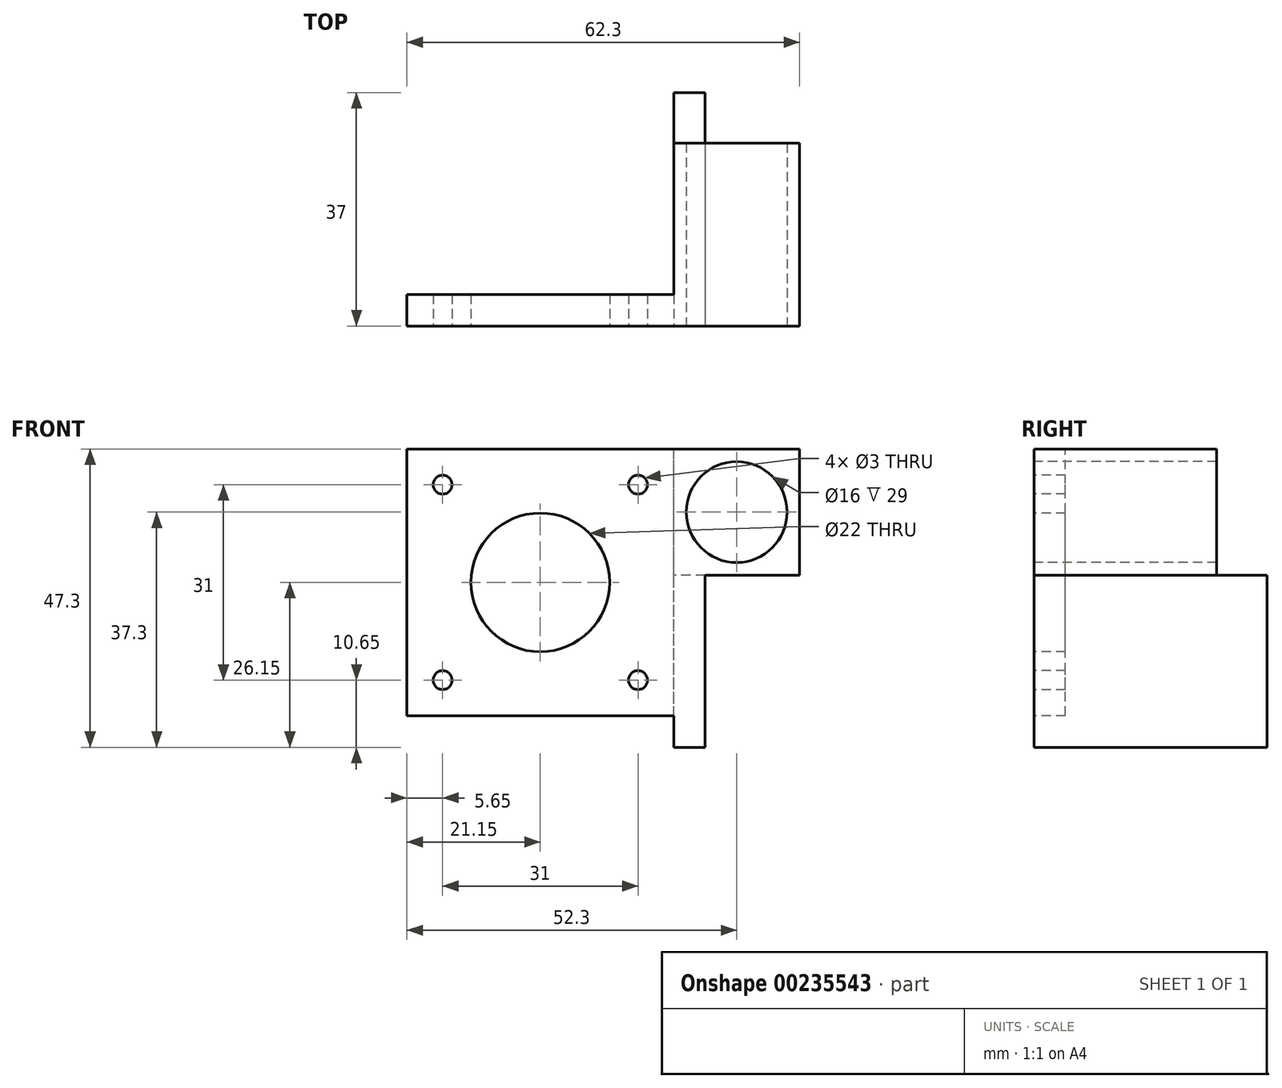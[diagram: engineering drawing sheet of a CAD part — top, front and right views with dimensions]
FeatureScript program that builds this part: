
annotation { "Feature Type Name" : "Feature", "Feature Type Description" : "" }
export const myFeature = defineFeature(function(context is Context, id is Id, definition is map)
    precondition{}
    {
        {
            var Q0;
            Q0=qCreatedBy(makeId("Front.planeOp"),FACE);
            var sketch = newSketch(context, id + "F0", { "sketchPlane" : qUnion([Q0])});
            skLineSegment(sketch, "E0.bottom", {"start": v(21.15, -21.15) * mm, "end": v(-21.15, -21.15) * mm});
            skLineSegment(sketch, "E0.top", {"start": v(20.15, 21.15) * mm, "end": v(-21.15, 21.15) * mm});
            skLineSegment(sketch, "E0.left", {"start": v(21.15, -21.15) * mm, "end": v(21.15, 20.15) * mm});
            skLineSegment(sketch, "E0.right", {"start": v(-21.15, -21.15) * mm, "end": v(-21.15, 21.15) * mm});
            skPoint(sketch, "E0.middle", {"position": v(0, 0) * mm});
            skLineSegment(sketch, "E1.bottom", {"start": v(15.5, -15.5) * mm, "end": v(-15.5, -15.5) * mm});
            skLineSegment(sketch, "E1.top", {"start": v(15.5, 15.5) * mm, "end": v(-15.5, 15.5) * mm});
            skLineSegment(sketch, "E1.left", {"start": v(15.5, -15.5) * mm, "end": v(15.5, 15.5) * mm});
            skLineSegment(sketch, "E1.right", {"start": v(-15.5, -15.5) * mm, "end": v(-15.5, 15.5) * mm});
            skCircle(sketch, "E2", {"center": v(-15.5, 15.5) * mm, "radius": 1.5 * mm});
            skCircle(sketch, "E3", {"center": v(15.5, 15.5) * mm, "radius": 1.5 * mm});
            skCircle(sketch, "E4", {"center": v(-15.5, -15.5) * mm, "radius": 1.5 * mm});
            skCircle(sketch, "E5", {"center": v(15.5, -15.5) * mm, "radius": 1.5 * mm});
            skLineSegment(sketch, "E6.bottom", {"start": v(-21.15, -21.15) * mm, "end": v(21.15, -21.15) * mm});
            skLineSegment(sketch, "E6.top", {"start": v(-21.15, -26.15) * mm, "end": v(21.15, -26.15) * mm});
            skLineSegment(sketch, "E6.left", {"start": v(-21.15, -21.15) * mm, "end": v(-21.15, -26.15) * mm});
            skLineSegment(sketch, "E6.right", {"start": v(21.15, -21.15) * mm, "end": v(21.15, -26.15) * mm});
            skCircle(sketch, "E7", {"center": v(0, 0) * mm, "radius": 11 * mm});
            skLineSegment(sketch, "E8.bottom", {"start": v(-21.15, 21.15) * mm, "end": v(20.15, 21.15) * mm});
            skLineSegment(sketch, "E8.top", {"start": v(-21.15, 26.15) * mm, "end": v(20.15, 26.15) * mm});
            skLineSegment(sketch, "E8.left", {"start": v(-21.15, 21.15) * mm, "end": v(-21.15, 26.15) * mm});
            skLineSegment(sketch, "E9.top", {"start": v(21.15, -26.15) * mm, "end": v(26.15, -26.15) * mm});
            skLineSegment(sketch, "E9.right", {"start": v(26.15, 1.15) * mm, "end": v(26.15, -26.15) * mm});
            skLineSegment(sketch, "E10.trimOffspring", {"start": v(21.15, 20.15) * mm, "end": v(21.15, -26.15) * mm});
            skLineSegment(sketch, "E11.top", {"start": v(20.15, 21.15) * mm, "end": v(21.15, 21.15) * mm});
            skLineSegment(sketch, "E11.right", {"start": v(21.15, 20.15) * mm, "end": v(21.15, 21.15) * mm});
            skLineSegment(sketch, "E12", {"start": v(20.15, 26.15) * mm, "end": v(26.15, 26.15) * mm});
            skLineSegment(sketch, "E13", {"start": v(26.15, 26.15) * mm, "end": v(26.15, 21.15) * mm});
            skLineSegment(sketch, "E14", {"start": v(21.15, 21.15) * mm, "end": v(26.15, 21.15) * mm});
            skLineSegment(sketch, "E15", {"start": v(26.15, 21.15) * mm, "end": v(41.15, 21.15) * mm});
            skLineSegment(sketch, "E16", {"start": v(41.15, 21.15) * mm, "end": v(41.15, 1.15) * mm});
            skLineSegment(sketch, "E17", {"start": v(41.15, 1.15) * mm, "end": v(26.15, 1.15) * mm});
            skCircle(sketch, "E18", {"center": v(31.15, 11.15) * mm, "radius": 8 * mm});
            skPoint(sketch, "E18.centerSnap0", {"position": v(41.15, 11.15) * mm});
            skPoint(sketch, "E18.centerSnap1", {"position": v(31.15, 21.15) * mm});
            skLineSegment(sketch, "E19", {"start": v(26.15, 1.15) * mm, "end": v(21.15, 1.15) * mm});
            skSolve(sketch);
        }
        {
            var Q0;
            {var subQ0=sQuery(id+"F0.wireOp",EDGE,"E6.bottom");Q0=makeQuery(id+"F0.imprint","IMPRINT",FACE,{"disambiguationData":[TD([[makeQuery(id+"F0.imprint","IMPRINT",EDGE,{"derivedFrom":subQ0}),-1.0]])]});}
            var Q1;
            {var subQ4=sQuery(id+"F0.wireOp",EDGE,"E15");Q1=makeQuery(id+"F0.imprint","IMPRINT",FACE,{"disambiguationData":[TD([[makeQuery(id+"F0.imprint","IMPRINT",EDGE,{"derivedFrom":subQ4}),-1.0]])]});}
            var Q2;
            {var subQ7=sQuery(id+"F0.wireOp",EDGE,"E9.top");Q2=makeQuery(id+"F0.imprint","IMPRINT",FACE,{"disambiguationData":[TD([[makeQuery(id+"F0.imprint","IMPRINT",EDGE,{"derivedFrom":subQ7}),1.0]])]});}
            var Q3;
            Q3=makeQuery(id+"F0.imprint","IMPRINT",FACE,{"disambiguationData":[TD([[makeQuery(id+"F0.imprint","IMPRINT",EDGE,{"derivedFrom":sQuery(id+"F0.wireOp",EDGE,"E0.right")}),-1.0]])]});
            var Q4;
            Q4=makeQuery(id+"F0.imprint","IMPRINT",FACE,{"disambiguationData":[TD([[makeQuery(id+"F0.imprint","IMPRINT",EDGE,{"derivedFrom":sQuery(id+"F0.wireOp",EDGE,"E7")}),-1.0]])]});
            extrude(context, id + "F1", {"entities" : qUnion([Q0, Q1, Q2, Q3, Q4]), "oppositeDirection" : true, "depth" : 5 * mm});
        }
        {
            var Q0;
            {var subQ0=sQuery(id+"F0.wireOp",EDGE,"E6.bottom");Q0=makeQuery(id+"F0.imprint","IMPRINT",FACE,{"disambiguationData":[TD([[makeQuery(id+"F0.imprint","IMPRINT",EDGE,{"derivedFrom":subQ0}),-1.0]])]});}
            var Q1;
            {var subQ7=sQuery(id+"F0.wireOp",EDGE,"E9.top");Q1=makeQuery(id+"F0.imprint","IMPRINT",FACE,{"disambiguationData":[TD([[makeQuery(id+"F0.imprint","IMPRINT",EDGE,{"derivedFrom":subQ7}),1.0]])]});}
            extrude(context, id + "F2", {"entities" : qUnion([Q0, Q1]), "operationType" : NewBodyOperationType.ADD, "oppositeDirection" : true, "depth" : 37 * mm});
        }
        {
            var Q0;
            {var subQ4=sQuery(id+"F0.wireOp",EDGE,"E15");Q0=makeQuery(id+"F0.imprint","IMPRINT",FACE,{"disambiguationData":[TD([[makeQuery(id+"F0.imprint","IMPRINT",EDGE,{"derivedFrom":subQ4}),-1.0]])]});}
            extrude(context, id + "F3", {"entities" : qUnion([Q0]), "operationType" : NewBodyOperationType.ADD, "oppositeDirection" : true, "depth" : 29 * mm});
        }
    });
